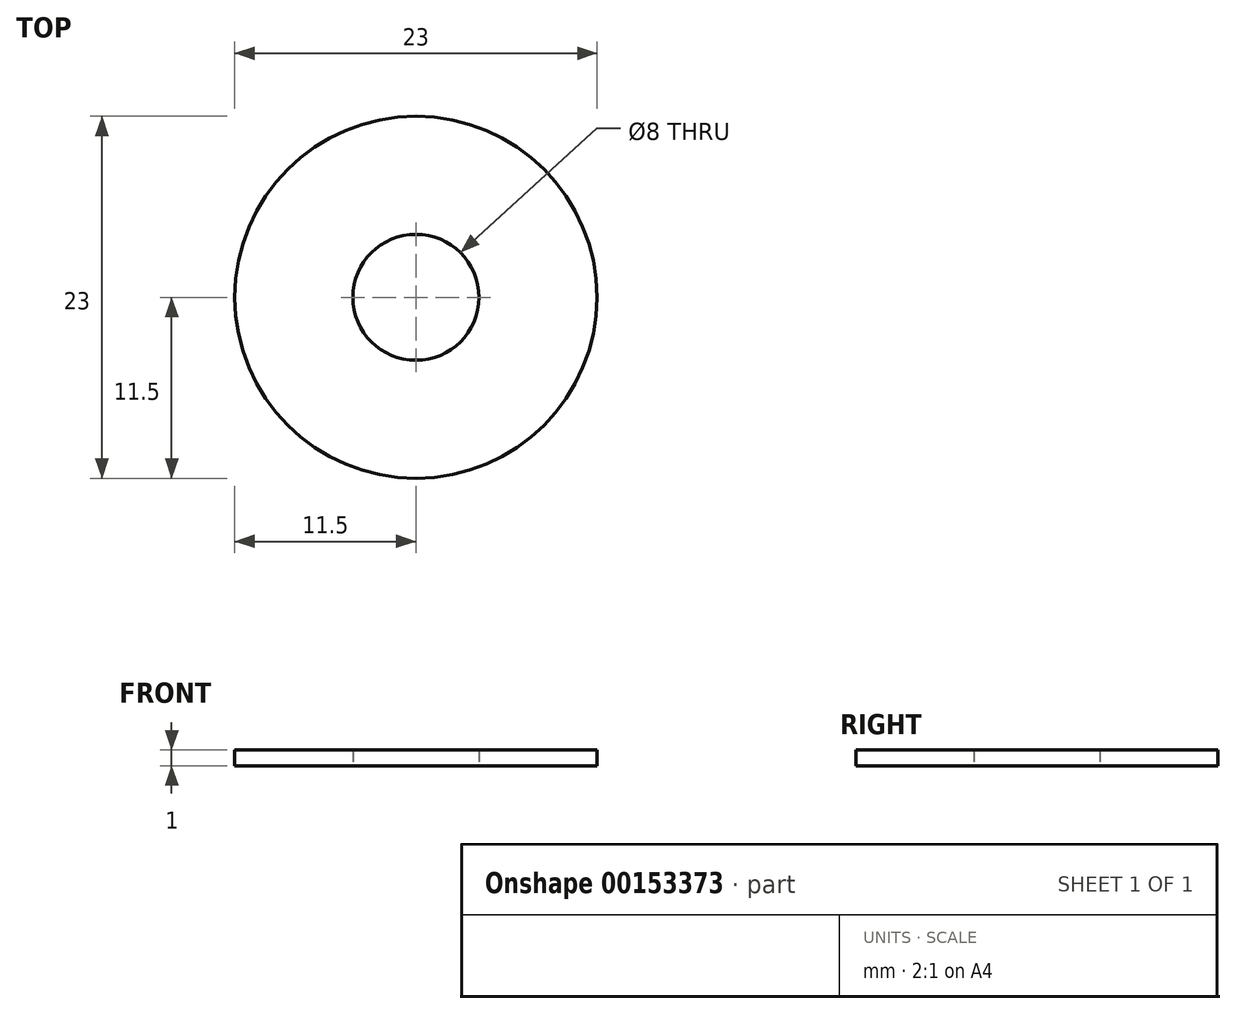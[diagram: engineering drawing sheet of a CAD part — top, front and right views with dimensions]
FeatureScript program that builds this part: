
annotation { "Feature Type Name" : "Feature", "Feature Type Description" : "" }
export const myFeature = defineFeature(function(context is Context, id is Id, definition is map)
    precondition{}
    {
        {
            var Q0;
            Q0=qCreatedBy(makeId("Top.planeOp"),FACE);
            var sketch = newSketch(context, id + "F0", { "sketchPlane" : qUnion([Q0])});
            skCircle(sketch, "E0", {"center": v(0, 0) * mm, "radius": 4 * mm});
            skCircle(sketch, "E1", {"center": v(0, 0) * mm, "radius": 11.5 * mm});
            skSolve(sketch);
        }
        {
            var Q0;
            Q0=qSketchRegion(id+"F0",true);
            extrude(context, id + "F1", {"entities" : qUnion([Q0]), "depth" : 1 * mm});
        }
    });
